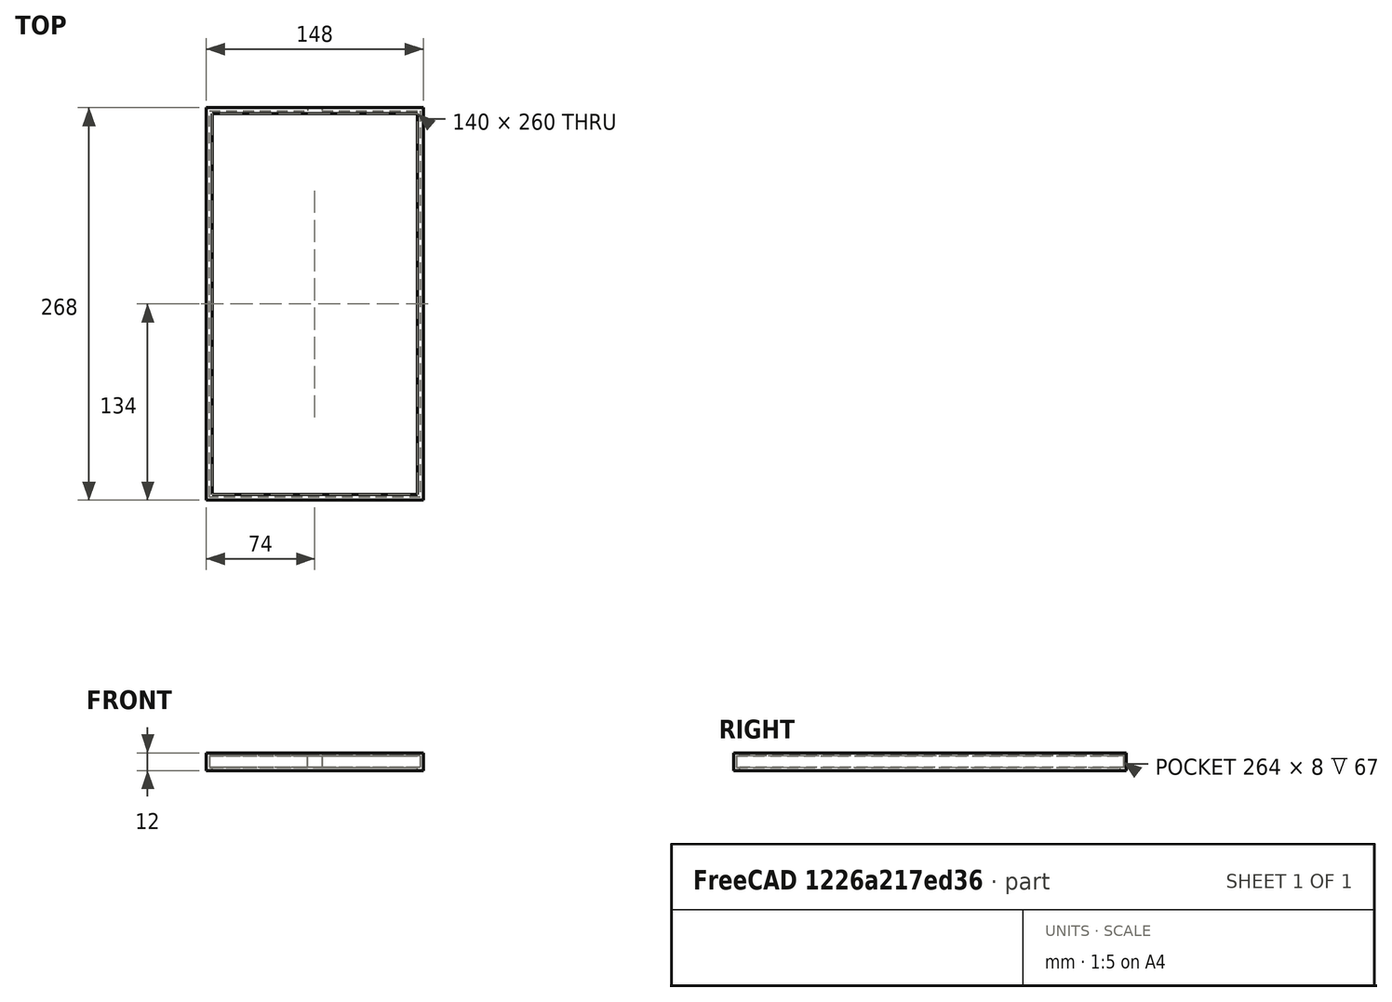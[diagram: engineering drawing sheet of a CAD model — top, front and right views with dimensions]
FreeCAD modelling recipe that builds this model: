
FCSTD DOCUMENT  (FreeCAD 0.21R33771 (Git))
Label: SataStripLine
License: All rights reserved
LicenseURL: http://en.wikipedia.org/wiki/All_rights_reserved
objects: Sketcher::SketchObject×3, PartDesign::Pocket×2, PartDesign::Pad×1, PartDesign::Body×1, Mesh::Feature×1
note: 10 computed .brp shape members not serialized (recipe doc carries the construction recipe); baked Part::Feature solids carry a one-line shape summary decoded from their .brp

FEATURE [Sketcher::SketchObject] Sketch  label="BaseTrackSketch"
  FullyConstrained = true
  MapMode = 5
  Support = -> [XY_Plane]
  sketch-geometry (10):
    g0: LineSegment StartX=-70 StartY=130 StartZ=0 EndX=-70 EndY=-130 EndZ=0
    g1: LineSegment StartX=-70 StartY=-130 StartZ=0 EndX=70 EndY=-130 EndZ=0
    g2: LineSegment StartX=70 StartY=-130 StartZ=0 EndX=70 EndY=130 EndZ=0
    g3: LineSegment StartX=70 StartY=130 StartZ=0 EndX=-70 EndY=130 EndZ=0
    g4: GeomPoint X=0 Y=0 Z=0
    g5: LineSegment StartX=-74 StartY=134 StartZ=0 EndX=-74 EndY=-134 EndZ=0
    g6: LineSegment StartX=-74 StartY=-134 StartZ=0 EndX=74 EndY=-134 EndZ=0
    g7: LineSegment StartX=74 StartY=-134 StartZ=0 EndX=74 EndY=134 EndZ=0
    g8: LineSegment StartX=74 StartY=134 StartZ=0 EndX=-74 EndY=134 EndZ=0
    g9: GeomPoint X=0 Y=0 Z=0
  constraints (24):
    c: Coincident(g0,g1)
    c: Coincident(g1,g2)
    c: Coincident(g2,g3)
    c: Coincident(g3,g0)
    c: Horizontal(g1)
    c: Horizontal(g3)
    c: Vertical(g0)
    c: Vertical(g2)
    c: Symmetric(g1,g0,g4)
    c: Coincident(g4,g-1)
    c: DistanceX(g0,g2) = 140
    c: DistanceY(g0,g0) = 260
    c: Coincident(g5,g6)
    c: Coincident(g6,g7)
    c: Coincident(g7,g8)
    c: Coincident(g8,g5)
    c: Horizontal(g6)
    c: Horizontal(g8)
    c: Vertical(g5)
    c: Vertical(g7)
    c: Symmetric(g6,g5,g9)
    c: Coincident(g9,g4)
    c: DistanceY(g0,g5) = 4
    c: DistanceX(g5,g0) = 4
FEATURE [PartDesign::Pad] Pad  label="BaseTrackPad"
  Direction = (0,0,1)
  Length = 12
  Length2 = 10
  Midplane = true
  Profile = -> Sketch
  ReferenceAxis = -> Sketch [N_Axis]
  Type = 0
FEATURE [Sketcher::SketchObject] Sketch001
  ExternalGeometry = -> [Pad]
  FullyConstrained = true
  MapMode = 5
  Support = -> [XY_Plane]
  sketch-geometry (6):
    g0: GeomPoint X=-72 Y=132 Z=0
    g1: GeomPoint X=72 Y=-132 Z=0
    g2: LineSegment StartX=-72 StartY=132 StartZ=0 EndX=72 EndY=132 EndZ=0
    g3: LineSegment StartX=72 StartY=132 StartZ=0 EndX=72 EndY=-132 EndZ=0
    g4: LineSegment StartX=72 StartY=-132 StartZ=0 EndX=-72 EndY=-132 EndZ=0
    g5: LineSegment StartX=-72 StartY=-132 StartZ=0 EndX=-72 EndY=132 EndZ=0
  constraints (12):
    c: Symmetric(g-3,g-4,g0)
    c: Symmetric(g-5,g-6,g1)
    c: Coincident(g2,g3)
    c: Coincident(g3,g4)
    c: Coincident(g4,g5)
    c: Coincident(g5,g2)
    c: Horizontal(g2)
    c: Horizontal(g4)
    c: Vertical(g3)
    c: Vertical(g5)
    c: Coincident(g2,g0)
    c: Coincident(g3,g1)
FEATURE [PartDesign::Pocket] Pocket
  BaseFeature = -> Pad
  Direction = (0,0,-1)
  Length = 8
  Length2 = 5
  Midplane = true
  Profile = -> Sketch001
  ReferenceAxis = -> Sketch001 [N_Axis]
  Type = 0
FEATURE [Sketcher::SketchObject] Sketch002
  FullyConstrained = true
  MapMode = 5
  Placement = pos=(0,134,0) rot=(0,0.707107,0.707107;3.14159rad)
  Support = -> [Pocket]
  sketch-geometry (5):
    g0: LineSegment StartX=-5 StartY=4 StartZ=0 EndX=-5 EndY=-4 EndZ=0
    g1: LineSegment StartX=-5 StartY=-4 StartZ=0 EndX=5 EndY=-4 EndZ=0
    g2: LineSegment StartX=5 StartY=-4 StartZ=0 EndX=5 EndY=4 EndZ=0
    g3: LineSegment StartX=5 StartY=4 StartZ=0 EndX=-5 EndY=4 EndZ=0
    g4: GeomPoint X=0 Y=0 Z=0
  constraints (12):
    c: Coincident(g0,g1)
    c: Coincident(g1,g2)
    c: Coincident(g2,g3)
    c: Coincident(g3,g0)
    c: Horizontal(g1)
    c: Horizontal(g3)
    c: Vertical(g0)
    c: Vertical(g2)
    c: Symmetric(g1,g0,g4)
    c: Coincident(g4,g-1)
    c: DistanceY(g2,g2) = 8
    c: DistanceX(g3,g3) = 10
FEATURE [PartDesign::Pocket] Pocket001
  BaseFeature = -> Pocket
  Direction = (0,-1,2e-16)
  Length = 5
  Length2 = 5
  Profile = -> Sketch002
  ReferenceAxis = -> Sketch002 [N_Axis]
  Type = 0
FEATURE [PartDesign::Body] Body  label="SataStrip"
  Group = -> [Sketch,Pad,Sketch001,Pocket,Sketch002,Pocket001]
  Origin = -> Origin
  Tip = -> Pocket001
FEATURE [Mesh::Feature] Mesh  label="SataStrip (Meshed)"
